# Revit family: 07742201(2019)
name_source: partatom
category: Plumbing Fixtures
revit_build: Autodesk Revit 2017 (Build: 20190508_0315(x64)
units: mm (PartAtom-declared; Revit-internal decimal feet)

## family parameters
Always vertical = Yes
Cut with Voids When Loaded = No
OmniClass Number = 23.45.55.00
OmniClass Title = Sanitary Faucets, Wastes
Part Type = Normal
Room Calculation Point = No
Round Connector Dimension = Use Diameter
Shared = No
Work Plane-Based = No

## types (1)
- 07742201 Washbasin faucet, 6 V
    2D/3D/BIM Files URL = http://static.hansa.com
    Advanced Features = Adjustable settings (with magnetic key);Waterways without nickel coating
    Aerator = Swivel aerator;CACHÉ® integrated aerator
    AssetType = Fixed
    Automatic Flush = off (off/12/24/48/72 h)
    Automatic Flush Period = 30 s (10-600 s)
    BIMObjectName = 07742201(2019)
    Battery = Lithium 2CR5 6 V, AA 1.5 V Lithium x 2, CR 2450 3 V
    BodyMaterial = Brass
    Brand = Hansa
    Catalog Drawing URL = http://static.hansa.com
    Category = Bathroom
    Class = Tiptronic, battery-operated, bidetta
    CloseOffRating = 0
    Color = Chrome/White
    Connection = Flexible Inlet Pipes
    Connection Size = G3/8
    ConvergoRefNr = 0087-1906-0018-FI
    Customs Code = 84818011
    Dimension Drawing URL = http://static.hansa.com
    DurationUnit = Year
    EAN Number = 4015470030415
    EMC Directive = 2004/108/EY
    EN Standard = EN 15091
    Electronic Parts = Low battery indication; Signal lights; Control unit
    Extensions = Rapid pop-up waste
    FDV Document URL = http://www.hansa.com
    FaucetMainMaterial = Brass
    FaucetNominalDepth = 170 mm  [stored 0.557743 ft]
    FaucetNominalHeight = 152 mm
    FaucetNominalWidth = 75 mm
    Features = Tiptronic, battery-operated
    Finish = Polished
    Flow Drawing URL = http://static.hansa.com
    Flow Rate At 300kPa With Flow Controller = 0.1 L/s
    FlowCoefficient = 0
    Group = Washbasin faucets
    Hand Shower = Remote operated Smart Bidetta
    HandShowerNominalDepth = 69 mm
    HandShowerNominalHeight = 318 mm
    HandShowerNominalWidth = 57 mm
    IfcExportAs = IfcValveType
    IfcExportType = FAUCET
    InletConnectionSize = 10 mm  [stored 0.0328084 ft]
    Installation Type = Deck mounted
    Installation and Maintenance = http://static.hansa.com
    Lever Handle = Temperature control handle
    ManufacterURL = http://www.hansa.com
    Manufacturer = Hansa
    ManufacturerName = Hansa
    Market = AUT;BEL;CZE;DEU;ESP;FRA;INT;NLD;SVK
    Material = Brass
    Max Flow Period = 6.0 s
    Max. Hot Water Supply = 70 °C
    Mechanical Parts = Mixing valve
    Model = 07742201 Washbasin faucet, 6 V
    ModelReference = 07742201
    Mounting Holes = 1 mounting hole
    NBSDescription = Water supply fittings for wash basin and troughs
    NBSReference = 45-35-70/371
    Name = 07742201 Washbasin faucet, 6 V
    Name_en = 07742201 Washbasin faucet, 6 V
    Noise Class = I (ISO 3822)
    Number of Shower Sprays = 1 spray
    Operating Voltage = 6 V
    Package Weight = 3.358 kg
    Package external Dimensions = 535 x 215 x 105
    Pipes = Flexible inlet pipe(s)
    Product Code = 07742201
    Product Datasheet = http://www.hansa.com
    Product Family = ALESSI Sense by HANSA
    Product Image URL = http://static.hansa.com
    Product URL = http://static.hansa.com
    Projection = 118 mm
    Protection Class = IP 44
    Revision = 2
    Shape = Sculptured
    Shower Parts = Shower Hose (1500 mm);Shower holder
    Size = Faucet: 75x170x150 mm / Hand shower: 55x70x320 mm
    Spare Parts = http://static.hansa.com
    Spout Type = Fixed spout
    Uniclass2 = Pr_40_30_96_96
    Uniclass2015Description = Washbasin manual water supply sets
    Uniclass2015Reference = Pr_40_20_87_96
    Version = 2
    VersionDate = 01/05/2020
    WarrantyDescription = http://warranty.hansa.com
    WarrantyDurationUnit = Year
    WorkingPressure = 100- 1000 kPa

note: [stored X ft] marks values corroborated as IEEE doubles in the binary element streams (Revit-internal decimal feet)

## geometry (parser evidence)
native form markers: Sweep x9
no freeform markers — native parametric forms only
